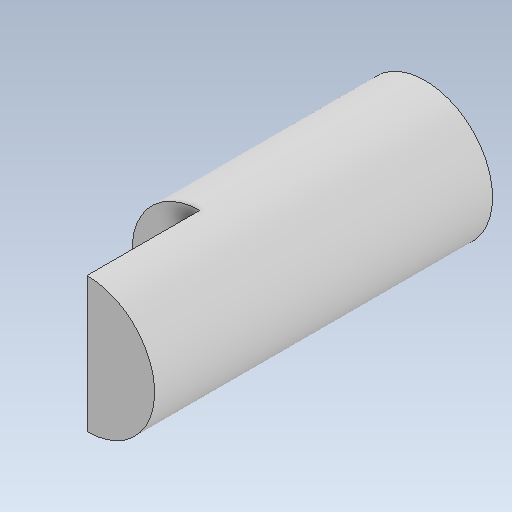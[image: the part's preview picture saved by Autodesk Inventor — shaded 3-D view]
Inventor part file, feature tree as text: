
AUTODESK INVENTOR PART (.ipt)
format: ipt  version: 2020 (Build 240168000, 168)  size: 99,328 bytes
history: native  units: mm
features: other x6, extrude x2, sketch x2
ambient origin geometry x8: Origin, YZ Plane, XZ Plane, XY Plane, X Axis, Y Axis, Z Axis, Center Point
bodies: Body1 (feature_tree)
feature tree (10):
  other  "Sólido1"
  extrude  "Extrusão1"  Depth=4.0mm TaperAngle=0.0deg
  extrude  "Extrusão2"  [1 undecoded]
  sketch  "Esboço1"  dims[d0=8.0mm d1=0.0mm d2=4.0mm d3=0.0mm]
  other  "Referência1"
  sketch  "Esboço2"
  other  "<userpath>\Desktop\rabo\3d\ela.iam"
  other  "ela.iam"
  other  "basesinha:1"
  other  "Component2:1"
note: 1 required parameter value undecoded (feature->parameter linkage not recoverable at this tier; creation-order binding heuristic only, values carry confidence <= 0.55)
